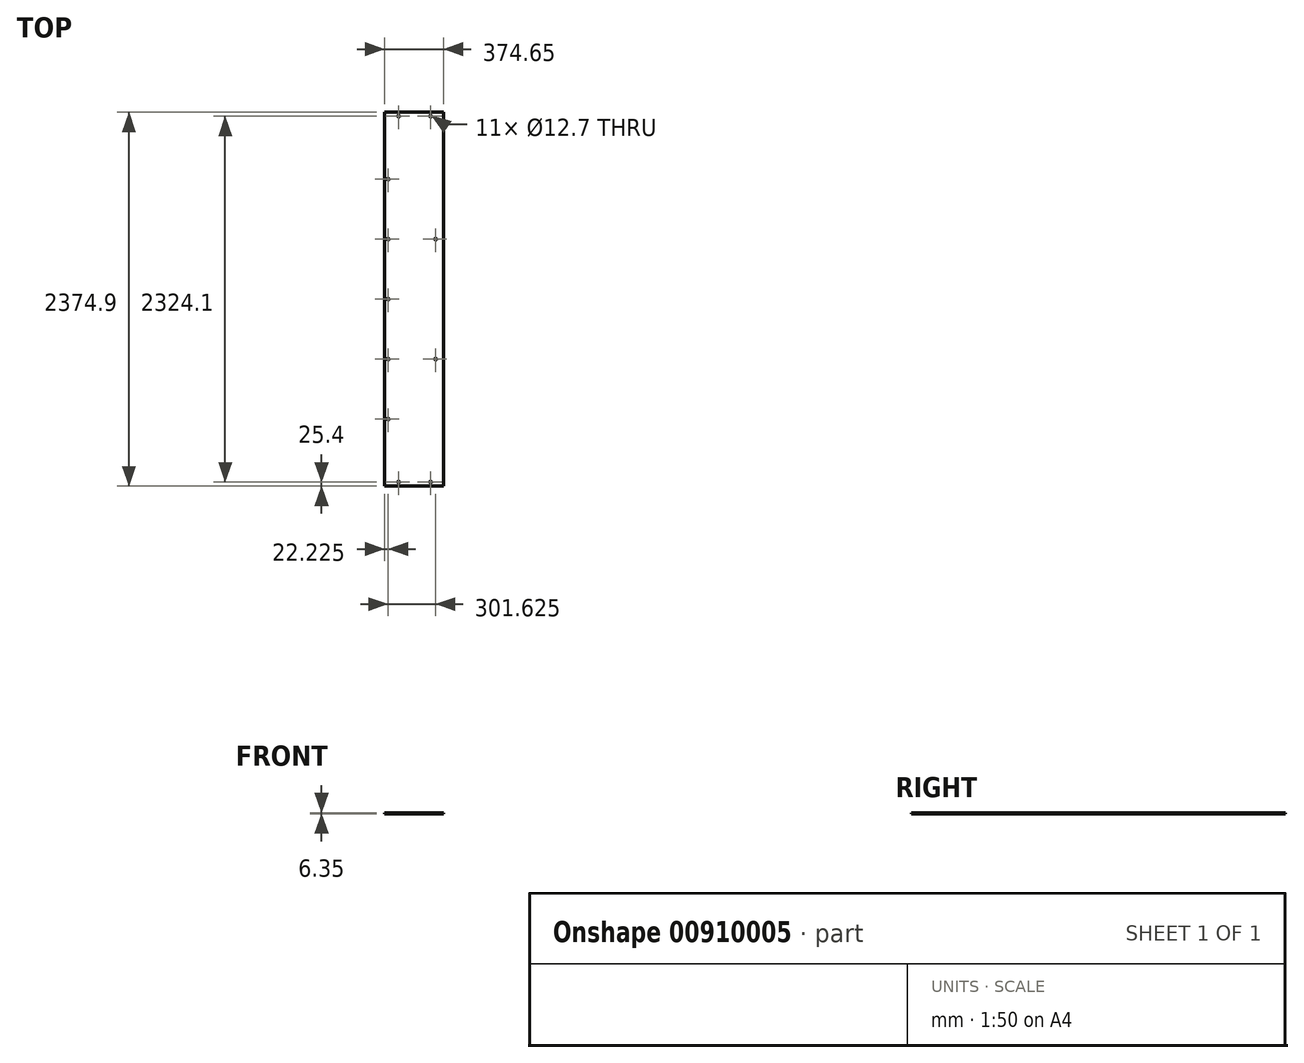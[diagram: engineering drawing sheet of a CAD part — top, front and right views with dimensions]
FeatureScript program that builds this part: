
annotation { "Feature Type Name" : "Feature", "Feature Type Description" : "" }
export const myFeature = defineFeature(function(context is Context, id is Id, definition is map)
    precondition{}
    {
        {
            var Q0;
            Q0=qCreatedBy(makeId("Front.planeOp"),FACE);
            var sketch = newSketch(context, id + "F0", { "sketchPlane" : qUnion([Q0])});
            skLineSegment(sketch, "E0.bottom", {"start": v(0, 6.35) * mm, "end": v(374.65, 6.35) * mm});
            skLineSegment(sketch, "E0.top", {"start": v(0, 0) * mm, "end": v(374.65, 0) * mm});
            skLineSegment(sketch, "E0.left", {"start": v(0, 6.35) * mm, "end": v(0, 0) * mm});
            skLineSegment(sketch, "E0.right", {"start": v(374.65, 6.35) * mm, "end": v(374.65, 0) * mm});
            skSolve(sketch);
        }
        {
            var Q0;
            Q0=makeQuery(id+"F0.imprint","IMPRINT",FACE,{"disambiguationData":[TD([[makeQuery(id+"F0.imprint","IMPRINT",EDGE,{"derivedFrom":sQuery(id+"F0.wireOp",EDGE,"E0.bottom")}),-1.0]])]});
            extrude(context, id + "F1", {"entities" : qUnion([Q0]), "depth" : 2374.9 * mm, "offsetDistance" : 25 * mm, "symmetric" : true});
        }
        {
            var Q0;
            Q0=makeQuery(id+"F1.opExtrude","SWEPT_FACE",FACE,{"disambiguationData":[OSD([sQuery(id+"F0.wireOp",EDGE,"E0.top")])]});
            var sketch = newSketch(context, id + "F2", { "sketchPlane" : qUnion([Q0])});
            skLineSegment(sketch, "E1.bottom", {"start": v(292.1, 1162.05) * mm, "end": v(88.9, 1162.05) * mm, "construction": true});
            skLineSegment(sketch, "E1.top", {"start": v(292.1, -1162.05) * mm, "end": v(88.9, -1162.05) * mm, "construction": true});
            skLineSegment(sketch, "E1.left", {"start": v(292.1, 1162.05) * mm, "end": v(292.1, -1162.05) * mm, "construction": true});
            skLineSegment(sketch, "E1.right", {"start": v(88.9, 1162.05) * mm, "end": v(88.9, -1162.05) * mm, "construction": true});
            skLineSegment(sketch, "E2", {"start": v(292.1, 0) * mm, "end": v(0, 0) * mm, "construction": true});
            skCircle(sketch, "E3", {"center": v(292.1, 1162.05) * mm, "radius": 6.35 * mm});
            skCircle(sketch, "E4", {"center": v(88.9, 1162.05) * mm, "radius": 6.35 * mm});
            skCircle(sketch, "E5", {"center": v(292.1, -1162.05) * mm, "radius": 6.35 * mm});
            skCircle(sketch, "E6", {"center": v(88.9, -1162.05) * mm, "radius": 6.35 * mm});
            skLineSegment(sketch, "E7", {"start": v(22.23, 381) * mm, "end": v(22.23, 0) * mm, "construction": true});
            skLineSegment(sketch, "E8", {"start": v(22.22, 0) * mm, "end": v(22.23, -381) * mm, "construction": true});
            skCircle(sketch, "E9", {"center": v(22.23, 381) * mm, "radius": 6.35 * mm});
            skCircle(sketch, "E10", {"center": v(22.23, -381) * mm, "radius": 6.35 * mm});
            skCircle(sketch, "E11", {"center": v(22.22, 0) * mm, "radius": 6.35 * mm});
            skLineSegment(sketch, "E12", {"start": v(22.23, -381) * mm, "end": v(22.23, -762) * mm, "construction": true});
            skLineSegment(sketch, "E13", {"start": v(22.23, 381) * mm, "end": v(22.22, 762) * mm, "construction": true});
            skCircle(sketch, "E14", {"center": v(22.23, -762) * mm, "radius": 6.35 * mm});
            skCircle(sketch, "E15", {"center": v(22.22, 762) * mm, "radius": 6.35 * mm});
            skLineSegment(sketch, "E16", {"start": v(22.23, -381) * mm, "end": v(323.85, -381) * mm, "construction": true});
            skLineSegment(sketch, "E17", {"start": v(22.23, 381) * mm, "end": v(323.85, 381) * mm, "construction": true});
            skCircle(sketch, "E18", {"center": v(323.85, -381) * mm, "radius": 6.35 * mm});
            skCircle(sketch, "E19", {"center": v(323.85, 381) * mm, "radius": 6.35 * mm});
            skSolve(sketch);
        }
        {
            var Q0;
            Q0=makeQuery(id+"F2.imprint","IMPRINT",FACE,{"disambiguationData":[TD([[makeQuery(id+"F2.imprint","IMPRINT",EDGE,{"derivedFrom":sQuery(id+"F2.wireOp",EDGE,"E3")}),1.0]])]});
            var Q1;
            Q1=makeQuery(id+"F2.imprint","IMPRINT",FACE,{"disambiguationData":[TD([[makeQuery(id+"F2.imprint","IMPRINT",EDGE,{"derivedFrom":sQuery(id+"F2.wireOp",EDGE,"E4")}),1.0]])]});
            var Q2;
            Q2=makeQuery(id+"F2.imprint","IMPRINT",FACE,{"disambiguationData":[TD([[makeQuery(id+"F2.imprint","IMPRINT",EDGE,{"derivedFrom":sQuery(id+"F2.wireOp",EDGE,"E5")}),1.0]])]});
            var Q3;
            Q3=makeQuery(id+"F2.imprint","IMPRINT",FACE,{"disambiguationData":[TD([[makeQuery(id+"F2.imprint","IMPRINT",EDGE,{"derivedFrom":sQuery(id+"F2.wireOp",EDGE,"E6")}),1.0]])]});
            var Q4;
            Q4=makeQuery(id+"F2.imprint","IMPRINT",FACE,{"disambiguationData":[TD([[makeQuery(id+"F2.imprint","IMPRINT",EDGE,{"derivedFrom":sQuery(id+"F2.wireOp",EDGE,"E9")}),1.0]])]});
            var Q5;
            Q5=makeQuery(id+"F2.imprint","IMPRINT",FACE,{"disambiguationData":[TD([[makeQuery(id+"F2.imprint","IMPRINT",EDGE,{"derivedFrom":sQuery(id+"F2.wireOp",EDGE,"E10")}),1.0]])]});
            var Q6;
            Q6=makeQuery(id+"F2.imprint","IMPRINT",FACE,{"disambiguationData":[TD([[makeQuery(id+"F2.imprint","IMPRINT",EDGE,{"derivedFrom":sQuery(id+"F2.wireOp",EDGE,"E15")}),1.0]])]});
            var Q7;
            Q7=makeQuery(id+"F2.imprint","IMPRINT",FACE,{"disambiguationData":[TD([[makeQuery(id+"F2.imprint","IMPRINT",EDGE,{"derivedFrom":sQuery(id+"F2.wireOp",EDGE,"E11")}),1.0]])]});
            var Q8;
            Q8=makeQuery(id+"F2.imprint","IMPRINT",FACE,{"disambiguationData":[TD([[makeQuery(id+"F2.imprint","IMPRINT",EDGE,{"derivedFrom":sQuery(id+"F2.wireOp",EDGE,"E14")}),1.0]])]});
            var Q9;
            Q9=makeQuery(id+"F2.imprint","IMPRINT",FACE,{"disambiguationData":[TD([[makeQuery(id+"F2.imprint","IMPRINT",EDGE,{"derivedFrom":sQuery(id+"F2.wireOp",EDGE,"E19")}),1.0]])]});
            var Q10;
            Q10=makeQuery(id+"F2.imprint","IMPRINT",FACE,{"disambiguationData":[TD([[makeQuery(id+"F2.imprint","IMPRINT",EDGE,{"derivedFrom":sQuery(id+"F2.wireOp",EDGE,"E18")}),1.0]])]});
            extrude(context, id + "F3", {"entities" : qUnion([Q0, Q1, Q2, Q3, Q4, Q5, Q6, Q7, Q8, Q9, Q10]), "operationType" : NewBodyOperationType.REMOVE, "endBound" : BoundingType.THROUGH_ALL, "oppositeDirection" : true, "depth" : 25 * mm, "offsetDistance" : 25 * mm});
        }
    });
